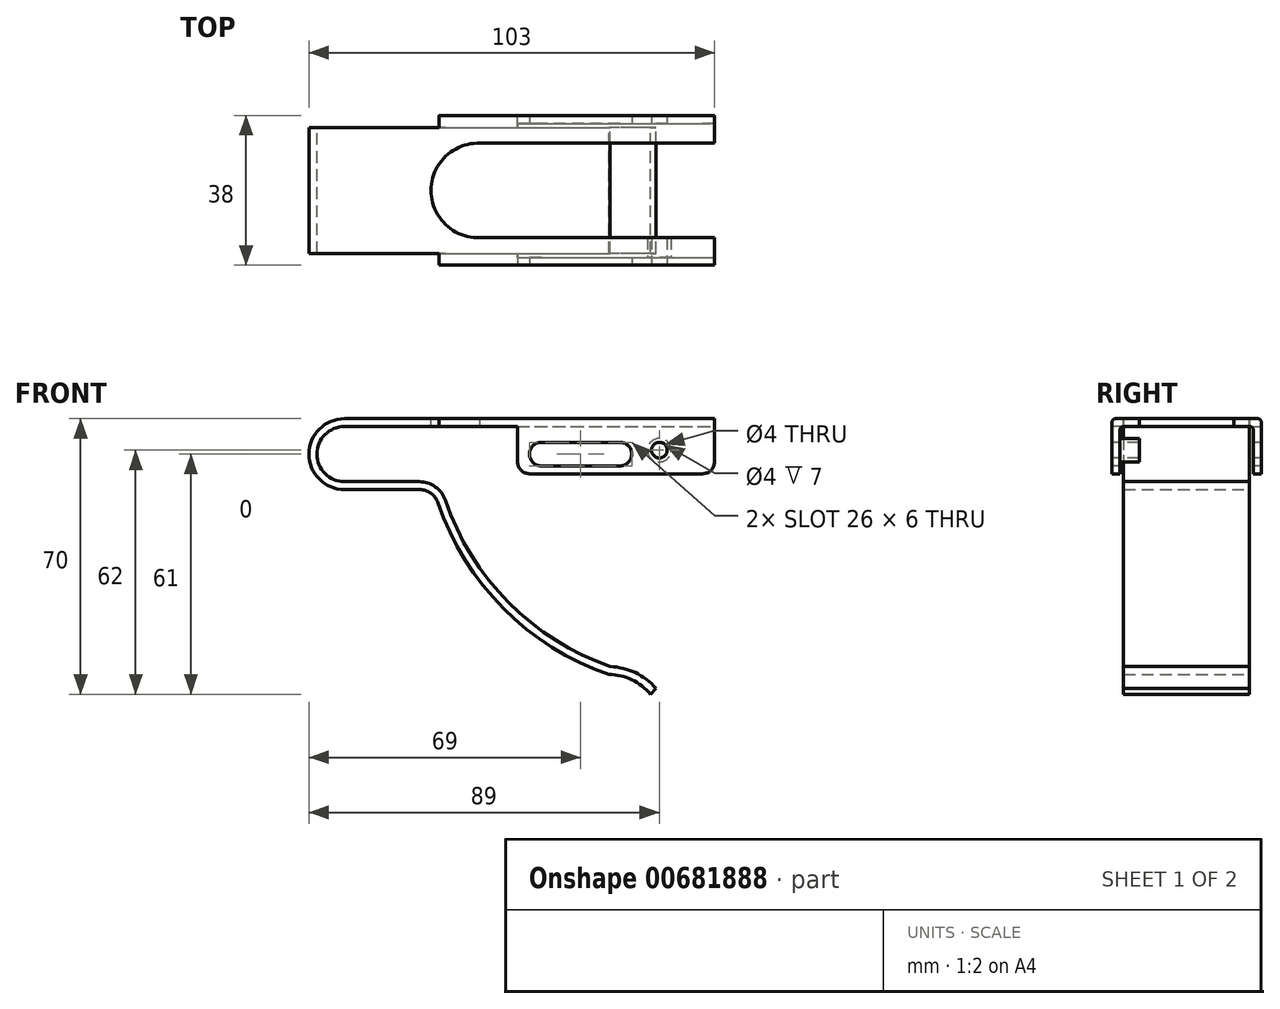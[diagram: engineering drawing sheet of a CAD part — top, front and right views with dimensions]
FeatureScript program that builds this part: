
annotation { "Feature Type Name" : "Feature", "Feature Type Description" : "" }
export const myFeature = defineFeature(function(context is Context, id is Id, definition is map)
    precondition{}
    {
        {
            var Q0;
            Q0=qCreatedBy(makeId("Front.planeOp"),FACE);
            var sketch = newSketch(context, id + "F0", { "sketchPlane" : qUnion([Q0])});
            skArc(sketch, "E0", {"start": v(0, 9) * mm, "mid": v(-9, 0) * mm, "end": v(0, -9) * mm});
            skLineSegment(sketch, "E1", {"start": v(0, 9) * mm, "end": v(94, 9) * mm});
            skLineSegment(sketch, "E2", {"start": v(0, -9) * mm, "end": v(19, -9) * mm});
            skArc(sketch, "E3", {"start": v(23.73, -12.39) * mm, "mid": v(40.4, -39.22) * mm, "end": v(67.15, -56) * mm});
            skArc(sketch, "E4", {"start": v(77.75, -61) * mm, "mid": v(73, -57.34) * mm, "end": v(67.15, -56) * mm});
            skPoint(sketch, "E5.visualSharp", {"position": v(22.67, -9) * mm});
            skArc(sketch, "E5.filletArc", {"start": v(23.73, -12.39) * mm, "mid": v(21.91, -9.93) * mm, "end": v(19, -9) * mm});
            skLineSegment(sketch, "E6.0", {"start": v(0, 7) * mm, "end": v(94, 7) * mm});
            skArc(sketch, "E6.1", {"start": v(0, 7) * mm, "mid": v(-7, 0) * mm, "end": v(0, -7) * mm});
            skArc(sketch, "E6.2", {"start": v(79.13, -59.5) * mm, "mid": v(73.9, -55.53) * mm, "end": v(67.5, -54) * mm});
            skArc(sketch, "E6.3", {"start": v(25.63, -11.74) * mm, "mid": v(41.7, -37.7) * mm, "end": v(67.5, -54) * mm});
            skArc(sketch, "E6.4", {"start": v(25.63, -11.74) * mm, "mid": v(23.08, -8.3) * mm, "end": v(19, -7) * mm});
            skLineSegment(sketch, "E6.5", {"start": v(0, -7) * mm, "end": v(19, -7) * mm});
            skLineSegment(sketch, "E7", {"start": v(94, 7) * mm, "end": v(94, 9) * mm});
            skLineSegment(sketch, "E8", {"start": v(77.75, -61) * mm, "end": v(79.13, -59.5) * mm});
            skSolve(sketch);
        }
        {
            var Q0;
            Q0 = qSketchRegion(id + "F0", true);
            extrude(context, id + "F1", {"entities" : qUnion([Q0]), "depth" : 16 * mm, "offsetDistance" : 25 * mm});
        }
        {
            var Q0;
            Q0=makeQuery(id+"F1.opExtrude","SWEPT_FACE",FACE,{"disambiguationData":[OSD([sQuery(id+"F0.wireOp",EDGE,"E1")])]});
            var sketch = newSketch(context, id + "F2", { "sketchPlane" : qUnion([Q0])});
            skLineSegment(sketch, "E9.bottom", {"start": v(24, -16) * mm, "end": v(94, -16) * mm});
            skLineSegment(sketch, "E9.top", {"start": v(24, -19) * mm, "end": v(94, -19) * mm});
            skLineSegment(sketch, "E9.left", {"start": v(24, -16) * mm, "end": v(24, -19) * mm});
            skLineSegment(sketch, "E9.right", {"start": v(94, -16) * mm, "end": v(94, -19) * mm});
            skSolve(sketch);
        }
        {
            var Q0;
            Q0 = qSketchRegion(id + "F2", true);
            extrude(context, id + "F3", {"entities" : qUnion([Q0]), "operationType" : NewBodyOperationType.ADD, "oppositeDirection" : true, "depth" : 2 * mm, "offsetDistance" : 25 * mm});
        }
        {
            var Q0;
            Q0=makeQuery(id+"F3.opExtrude","SWEPT_FACE",FACE,{"disambiguationData":[OSD([sQuery(id+"F2.wireOp",EDGE,"E9.top")])]});
            var sketch = newSketch(context, id + "F4", { "sketchPlane" : qUnion([Q0])});
            skLineSegment(sketch, "E10.bottom", {"start": v(44, 9) * mm, "end": v(94, 9) * mm});
            skLineSegment(sketch, "E10.top", {"start": v(44, -5) * mm, "end": v(94, -5) * mm});
            skLineSegment(sketch, "E10.left", {"start": v(44, 9) * mm, "end": v(44, -5) * mm});
            skLineSegment(sketch, "E10.right", {"start": v(94, 9) * mm, "end": v(94, -5) * mm});
            skSolve(sketch);
        }
        {
            var Q0;
            Q0 = qSketchRegion(id + "F4", true);
            extrude(context, id + "F5", {"entities" : qUnion([Q0]), "operationType" : NewBodyOperationType.ADD, "oppositeDirection" : true, "depth" : 2 * mm, "offsetDistance" : 25 * mm});
        }
        {
            var Q0;
            Q0=makeQuery(id+"F5.boolean.opBoolean","INTERSECT",EDGE,{"derivedFrom":[makeQuery(id+"F3.boolean.opBoolean","MERGE",FACE,{"derivedFrom":[makeQuery(id+"F1.opExtrude","SWEPT_FACE",FACE,{"disambiguationData":[OSD([sQuery(id+"F0.wireOp",EDGE,"E6.0")])]}),makeQuery(id+"F3.opExtrude","CAP_FACE",FACE,{"disambiguationData":[OSD([sQuery(id+"F2.wireOp",EDGE,"E9.bottom"),sQuery(id+"F2.wireOp",EDGE,"E9.top"),sQuery(id+"F2.wireOp",EDGE,"E9.left"),sQuery(id+"F2.wireOp",EDGE,"E9.right")])],"isStart":false})]}),makeQuery(id+"F5.opExtrude","CAP_FACE",FACE,{"disambiguationData":[OSD([sQuery(id+"F4.wireOp",EDGE,"E10.bottom"),sQuery(id+"F4.wireOp",EDGE,"E10.top"),sQuery(id+"F4.wireOp",EDGE,"E10.left"),sQuery(id+"F4.wireOp",EDGE,"E10.right")])],"isStart":false})]});
            var Q1;
            Q1=makeQuery(id+"F3.opExtrude","CAP_EDGE",EDGE,{"disambiguationData":[OSD([sQuery(id+"F2.wireOp",EDGE,"E9.top")])],"isStart":true});
            fillet(context, id + "F6", {"entities" : qUnion([Q0, Q1]), "radius" : 1 * mm, "allowEdgeOverflow" : false});
        }
        {
            var Q0;
            Q0=makeQuery(id+"F1.opExtrude","SWEPT_BODY",BODY,{"disambiguationData":[OSD([sQuery(id+"F0.wireOp",EDGE,"E0"),sQuery(id+"F0.wireOp",EDGE,"E1"),sQuery(id+"F0.wireOp",EDGE,"E2"),sQuery(id+"F0.wireOp",EDGE,"E3"),sQuery(id+"F0.wireOp",EDGE,"E4"),sQuery(id+"F0.wireOp",EDGE,"E5.filletArc"),sQuery(id+"F0.wireOp",EDGE,"E6.0"),sQuery(id+"F0.wireOp",EDGE,"E6.1"),sQuery(id+"F0.wireOp",EDGE,"E6.2"),sQuery(id+"F0.wireOp",EDGE,"E6.3"),sQuery(id+"F0.wireOp",EDGE,"E6.4"),sQuery(id+"F0.wireOp",EDGE,"E6.5"),sQuery(id+"F0.wireOp",EDGE,"E7"),sQuery(id+"F0.wireOp",EDGE,"E8")])]});
            var Q1;
            Q1=makeQuery(id+"F1.opExtrude","CAP_FACE",FACE,{"disambiguationData":[OSD([sQuery(id+"F0.wireOp",EDGE,"E0"),sQuery(id+"F0.wireOp",EDGE,"E1"),sQuery(id+"F0.wireOp",EDGE,"E2"),sQuery(id+"F0.wireOp",EDGE,"E3"),sQuery(id+"F0.wireOp",EDGE,"E4"),sQuery(id+"F0.wireOp",EDGE,"E5.filletArc"),sQuery(id+"F0.wireOp",EDGE,"E6.0"),sQuery(id+"F0.wireOp",EDGE,"E6.1"),sQuery(id+"F0.wireOp",EDGE,"E6.2"),sQuery(id+"F0.wireOp",EDGE,"E6.3"),sQuery(id+"F0.wireOp",EDGE,"E6.4"),sQuery(id+"F0.wireOp",EDGE,"E6.5"),sQuery(id+"F0.wireOp",EDGE,"E7"),sQuery(id+"F0.wireOp",EDGE,"E8")])],"isStart":true});
            mirror(context, id + "F7", {"operationType" : NewBodyOperationType.ADD, "entities" : qUnion([Q0]), "mirrorPlane" : qUnion([Q1])});
        }
        {
            var Q0;
            {var subQ0=makeQuery(id+"F3.boolean.opBoolean","MERGE",FACE,{"derivedFrom":[makeQuery(id+"F1.opExtrude","SWEPT_FACE",FACE,{"disambiguationData":[OSD([sQuery(id+"F0.wireOp",EDGE,"E1")])]}),makeQuery(id+"F3.opExtrude","CAP_FACE",FACE,{"disambiguationData":[OSD([sQuery(id+"F2.wireOp",EDGE,"E9.bottom"),sQuery(id+"F2.wireOp",EDGE,"E9.top"),sQuery(id+"F2.wireOp",EDGE,"E9.left"),sQuery(id+"F2.wireOp",EDGE,"E9.right")])],"isStart":true})]});Q0=makeQuery(id+"F7.boolean.opBoolean","MERGE",FACE,{"derivedFrom":[subQ0,makeQuery(id+"F7.opPattern","COPY",FACE,{"derivedFrom":subQ0,"instanceName":"1"})]});}
            var sketch = newSketch(context, id + "F8", { "sketchPlane" : qUnion([Q0])});
            skArc(sketch, "E11", {"start": v(34.5, 11.99) * mm, "mid": v(22, 0) * mm, "end": v(34.48, -12) * mm});
            skLineSegment(sketch, "E12", {"start": v(34.5, 11.99) * mm, "end": v(94, 11.99) * mm});
            skLineSegment(sketch, "E13", {"start": v(34.48, -12) * mm, "end": v(94, -12) * mm});
            skLineSegment(sketch, "E14", {"start": v(94, 11.99) * mm, "end": v(94, -12) * mm});
            skSolve(sketch);
        }
        {
            var Q0;
            Q0 = qSketchRegion(id + "F8", true);
            extrude(context, id + "F9", {"entities" : qUnion([Q0]), "operationType" : NewBodyOperationType.REMOVE, "oppositeDirection" : true, "depth" : 2 * mm, "offsetDistance" : 25 * mm});
        }
        {
            var Q0;
            Q0=makeQuery(id+"F5.boolean.opBoolean","MERGE",FACE,{"derivedFrom":[makeQuery(id+"F3.opExtrude","SWEPT_FACE",FACE,{"disambiguationData":[OSD([sQuery(id+"F2.wireOp",EDGE,"E9.top")])]}),makeQuery(id+"F5.opExtrude","CAP_FACE",FACE,{"disambiguationData":[OSD([sQuery(id+"F4.wireOp",EDGE,"E10.bottom"),sQuery(id+"F4.wireOp",EDGE,"E10.top"),sQuery(id+"F4.wireOp",EDGE,"E10.left"),sQuery(id+"F4.wireOp",EDGE,"E10.right")])],"isStart":true})]});
            var sketch = newSketch(context, id + "F10", { "sketchPlane" : qUnion([Q0])});
            skLineSegment(sketch, "E15", {"start": v(50, 0) * mm, "end": v(70, 0) * mm});
            skArc(sketch, "E16.0.startCap", {"start": v(50, -3) * mm, "mid": v(47, 0) * mm, "end": v(50, 3) * mm});
            skArc(sketch, "E16.0.endCap", {"start": v(70, 3) * mm, "mid": v(73, 0) * mm, "end": v(70, -3) * mm});
            skLineSegment(sketch, "E16.0.left", {"start": v(50, 3) * mm, "end": v(70, 3) * mm});
            skLineSegment(sketch, "E16.0.right", {"start": v(50, -3) * mm, "end": v(70, -3) * mm});
            skSolve(sketch);
        }
        {
            var Q0;
            Q0 = qSketchRegion(id + "F10", true);
            extrude(context, id + "F11", {"entities" : qUnion([Q0]), "operationType" : NewBodyOperationType.REMOVE, "endBound" : BoundingType.THROUGH_ALL, "oppositeDirection" : true, "depth" : 25 * mm, "offsetDistance" : 25 * mm});
        }
        {
            var Q0;
            Q0=makeQuery(id+"F5.boolean.opBoolean","MERGE",FACE,{"derivedFrom":[makeQuery(id+"F3.opExtrude","SWEPT_FACE",FACE,{"disambiguationData":[OSD([sQuery(id+"F2.wireOp",EDGE,"E9.top")])]}),makeQuery(id+"F5.opExtrude","CAP_FACE",FACE,{"disambiguationData":[OSD([sQuery(id+"F4.wireOp",EDGE,"E10.bottom"),sQuery(id+"F4.wireOp",EDGE,"E10.top"),sQuery(id+"F4.wireOp",EDGE,"E10.left"),sQuery(id+"F4.wireOp",EDGE,"E10.right")])],"isStart":true})]});
            var sketch = newSketch(context, id + "F12", { "sketchPlane" : qUnion([Q0])});
            skPoint(sketch, "E17", {"position": v(80, 1) * mm});
            skSolve(sketch);
        }
        {
            var Q0;
            Q0=sQuery(id+"F12.wireOp",VERTEX,"E17");
            var Q1;
            Q1=makeQuery(id+"F1.opExtrude","SWEPT_BODY",BODY,{"disambiguationData":[OSD([sQuery(id+"F0.wireOp",EDGE,"E0"),sQuery(id+"F0.wireOp",EDGE,"E1"),sQuery(id+"F0.wireOp",EDGE,"E2"),sQuery(id+"F0.wireOp",EDGE,"E3"),sQuery(id+"F0.wireOp",EDGE,"E4"),sQuery(id+"F0.wireOp",EDGE,"E5.filletArc"),sQuery(id+"F0.wireOp",EDGE,"E6.0"),sQuery(id+"F0.wireOp",EDGE,"E6.1"),sQuery(id+"F0.wireOp",EDGE,"E6.2"),sQuery(id+"F0.wireOp",EDGE,"E6.3"),sQuery(id+"F0.wireOp",EDGE,"E6.4"),sQuery(id+"F0.wireOp",EDGE,"E6.5"),sQuery(id+"F0.wireOp",EDGE,"E7"),sQuery(id+"F0.wireOp",EDGE,"E8")])]});
            hole(context, id + "F13", {"style" : HoleStyle.SIMPLE, "endStyle" : HoleEndStyle.THROUGH, "holeDiameter" : 4 * mm, "majorDiameter" : 5 * mm, "isTappedThrough" : true, "tappedDepth" : 12 * mm, "tapClearance" : 3, "locations" : qUnion([Q0]), "scope" : qUnion([Q1])});
        }
        {
            var Q0;
            Q0=makeQuery(id+"F5.opExtrude","CAP_FACE",FACE,{"disambiguationData":[OSD([sQuery(id+"F4.wireOp",EDGE,"E10.bottom"),sQuery(id+"F4.wireOp",EDGE,"E10.top"),sQuery(id+"F4.wireOp",EDGE,"E10.left"),sQuery(id+"F4.wireOp",EDGE,"E10.right")])],"isStart":false});
            var sketch = newSketch(context, id + "F14", { "sketchPlane" : qUnion([Q0])});
            skCircle(sketch, "E18.0", {"center": v(-80, 1) * mm, "radius": 2 * mm});
            skCircle(sketch, "E19.0", {"center": v(-80, 1) * mm, "radius": 3 * mm});
            skSolve(sketch);
        }
        {
            var Q0;
            Q0 = qSketchRegion(id + "F14", true);
            extrude(context, id + "F15", {"entities" : qUnion([Q0]), "operationType" : NewBodyOperationType.ADD, "depth" : 5 * mm, "offsetDistance" : 25 * mm});
        }
        {
            var Q0;
            Q0=makeQuery(id+"F7.opPattern","COPY",EDGE,{"derivedFrom":makeQuery(id+"F5.opExtrude","SWEPT_EDGE",EDGE,{"disambiguationData":[OSD([sQuery(id+"F4.wireOp",EDGE,"E10.top"),sQuery(id+"F4.wireOp",EDGE,"E10.right")])]}),"instanceName":"1"});
            var Q1;
            Q1=makeQuery(id+"F5.opExtrude","SWEPT_EDGE",EDGE,{"disambiguationData":[OSD([sQuery(id+"F4.wireOp",EDGE,"E10.top"),sQuery(id+"F4.wireOp",EDGE,"E10.right")])]});
            var Q2;
            Q2=makeQuery(id+"F5.opExtrude","SWEPT_EDGE",EDGE,{"disambiguationData":[OSD([sQuery(id+"F4.wireOp",EDGE,"E10.top"),sQuery(id+"F4.wireOp",EDGE,"E10.left")])]});
            var Q3;
            Q3=makeQuery(id+"F7.opPattern","COPY",EDGE,{"derivedFrom":makeQuery(id+"F5.opExtrude","SWEPT_EDGE",EDGE,{"disambiguationData":[OSD([sQuery(id+"F4.wireOp",EDGE,"E10.top"),sQuery(id+"F4.wireOp",EDGE,"E10.left")])]}),"instanceName":"1"});
            fillet(context, id + "F16", {"entities" : qUnion([Q0, Q1, Q2, Q3]), "radius" : 3 * mm, "tangentPropagation" : true, "allowEdgeOverflow" : false});
        }
    });
